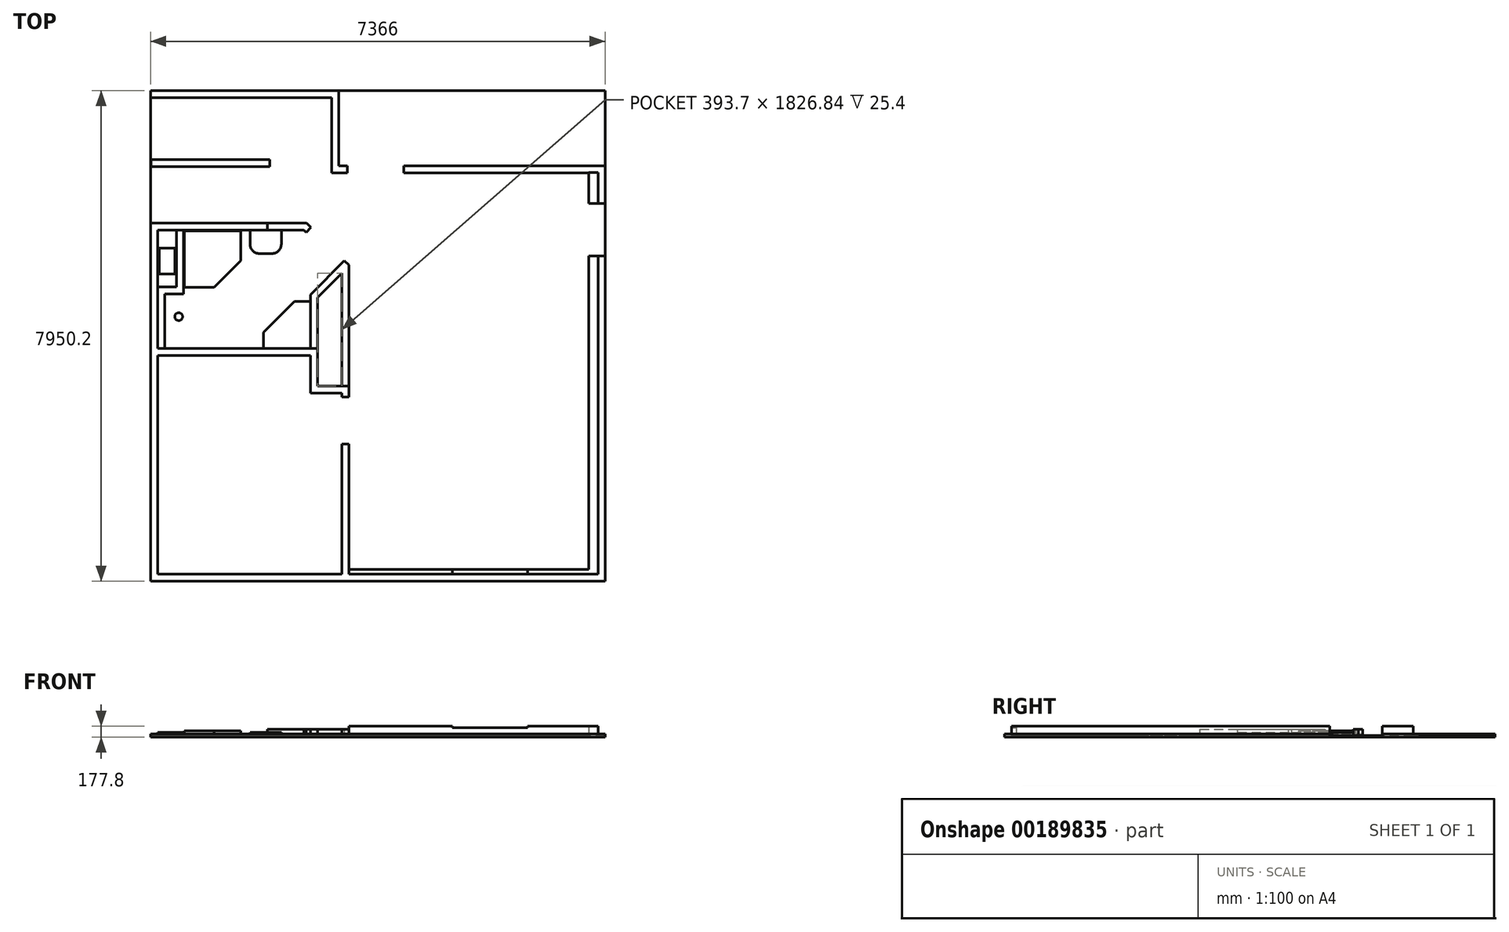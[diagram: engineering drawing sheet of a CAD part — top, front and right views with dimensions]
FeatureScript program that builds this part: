
annotation { "Feature Type Name" : "Feature", "Feature Type Description" : "" }
export const myFeature = defineFeature(function(context is Context, id is Id, definition is map)
    precondition{}
    {
        {
            var Q0;
            Q0=qCreatedBy(makeId("Top.planeOp"),FACE);
            var sketch = newSketch(context, id + "F0", { "sketchPlane" : qUnion([Q0])});
            skLineSegment(sketch, "E0.bottom", {"start": v(0, 0) * mm, "end": v(-7366, 0) * mm});
            skLineSegment(sketch, "E0.top", {"start": v(0, 7950.2) * mm, "end": v(-7366, 7950.2) * mm});
            skLineSegment(sketch, "E0.left", {"start": v(0, 0) * mm, "end": v(0, 7950.2) * mm});
            skLineSegment(sketch, "E0.right", {"start": v(-7366, 0) * mm, "end": v(-7366, 7950.2) * mm});
            skSolve(sketch);
        }
        {
            var Q0;
            Q0=qSketchRegion(id+"F0",true);
            extrude(context, id + "F1", {"entities" : qUnion([Q0]), "depth" : 25.4 * mm});
        }
        {
            var Q0;
            Q0=makeQuery(id+"F1.opExtrude","CAP_FACE",FACE,{"disambiguationData":[OSD([sQuery(id+"F0.wireOp",EDGE,"E0.bottom"),sQuery(id+"F0.wireOp",EDGE,"E0.top"),sQuery(id+"F0.wireOp",EDGE,"E0.left"),sQuery(id+"F0.wireOp",EDGE,"E0.right")])],"isStart":false});
            var sketch = newSketch(context, id + "F2", { "sketchPlane" : qUnion([Q0])});
            skLineSegment(sketch, "E1", {"start": v(0, 0) * mm, "end": v(0, 5270.5) * mm});
            skLineSegment(sketch, "E2", {"start": v(0, 5270.5) * mm, "end": v(-114.3, 5270.5) * mm});
            skLineSegment(sketch, "E3", {"start": v(-114.3, 5270.5) * mm, "end": v(-114.3, 114.3) * mm});
            skLineSegment(sketch, "E4", {"start": v(-114.3, 114.3) * mm, "end": v(-4152.9, 114.3) * mm});
            skLineSegment(sketch, "E5", {"start": v(-4152.9, 114.3) * mm, "end": v(-4152.9, 2222.5) * mm});
            skLineSegment(sketch, "E6", {"start": v(-4152.9, 2222.5) * mm, "end": v(-4267.2, 2222.5) * mm});
            skLineSegment(sketch, "E7", {"start": v(-4267.2, 2222.5) * mm, "end": v(-4267.2, 114.3) * mm});
            skLineSegment(sketch, "E8", {"start": v(-4267.2, 114.3) * mm, "end": v(-7251.7, 114.3) * mm});
            skLineSegment(sketch, "E9", {"start": v(0, 6121.4) * mm, "end": v(0, 6731) * mm});
            skLineSegment(sketch, "E10", {"start": v(0, 6731) * mm, "end": v(-3263.9, 6731) * mm});
            skLineSegment(sketch, "E11", {"start": v(0, 6121.4) * mm, "end": v(-114.3, 6121.4) * mm});
            skLineSegment(sketch, "E12", {"start": v(-114.3, 6121.4) * mm, "end": v(-114.3, 6616.7) * mm});
            skLineSegment(sketch, "E13", {"start": v(-114.3, 6616.7) * mm, "end": v(-3263.9, 6616.7) * mm});
            skLineSegment(sketch, "E14", {"start": v(-3263.9, 6731) * mm, "end": v(-3263.9, 6616.7) * mm});
            skLineSegment(sketch, "E15", {"start": v(-4152.9, 2984.5) * mm, "end": v(-4152.9, 3162.3) * mm});
            skLineSegment(sketch, "E16", {"start": v(-4152.9, 3162.3) * mm, "end": v(-4660.9, 3162.3) * mm});
            skLineSegment(sketch, "E17", {"start": v(-4660.9, 3162.3) * mm, "end": v(-4660.9, 3771.9) * mm});
            skLineSegment(sketch, "E18", {"start": v(-4660.9, 3771.9) * mm, "end": v(-7251.7, 3771.9) * mm});
            skLineSegment(sketch, "E19", {"start": v(-4152.9, 2984.5) * mm, "end": v(-4267.2, 2984.5) * mm});
            skLineSegment(sketch, "E20", {"start": v(-4267.2, 2984.5) * mm, "end": v(-4267.2, 3048) * mm});
            skLineSegment(sketch, "E21", {"start": v(-4267.2, 3048) * mm, "end": v(-4775.2, 3048) * mm});
            skLineSegment(sketch, "E22", {"start": v(-4775.2, 3048) * mm, "end": v(-4775.2, 3657.6) * mm});
            skLineSegment(sketch, "E23", {"start": v(-4775.2, 3657.6) * mm, "end": v(-7251.7, 3657.6) * mm});
            skLineSegment(sketch, "E24", {"start": v(-7251.7, 3771.9) * mm, "end": v(-7251.7, 5689.6) * mm});
            skLineSegment(sketch, "E25", {"start": v(-7251.7, 5689.6) * mm, "end": v(-5473.7, 5689.6) * mm});
            skLineSegment(sketch, "E26", {"start": v(-7366, 3657.6) * mm, "end": v(-7366, 5803.9) * mm});
            skLineSegment(sketch, "E27", {"start": v(-7366, 5803.9) * mm, "end": v(-5473.7, 5803.9) * mm});
            skLineSegment(sketch, "E28", {"start": v(-5473.7, 5689.6) * mm, "end": v(-5473.7, 5803.9) * mm});
            skLineSegment(sketch, "E29", {"start": v(-4178.3, 6616.7) * mm, "end": v(-4432.3, 6616.7) * mm});
            skLineSegment(sketch, "E30", {"start": v(-4432.3, 6616.7) * mm, "end": v(-4432.3, 7835.9) * mm});
            skLineSegment(sketch, "E31", {"start": v(-4432.3, 7835.9) * mm, "end": v(-7362.92, 7835.9) * mm});
            skLineSegment(sketch, "E32", {"start": v(-4178.3, 6616.7) * mm, "end": v(-4178.3, 6731) * mm});
            skLineSegment(sketch, "E33", {"start": v(-4178.3, 6731) * mm, "end": v(-4318, 6731) * mm});
            skLineSegment(sketch, "E34", {"start": v(-4318, 6731) * mm, "end": v(-4318, 7950.2) * mm});
            skLineSegment(sketch, "E35", {"start": v(-4318, 7950.2) * mm, "end": v(-7362.92, 7950.2) * mm});
            skLineSegment(sketch, "E36.bottom", {"start": v(-7359.96, 6832.6) * mm, "end": v(-5435.6, 6832.6) * mm});
            skLineSegment(sketch, "E36.top", {"start": v(-7359.96, 6718.3) * mm, "end": v(-5435.6, 6718.3) * mm});
            skLineSegment(sketch, "E36.left", {"start": v(-7359.96, 6832.6) * mm, "end": v(-7359.96, 6718.3) * mm});
            skLineSegment(sketch, "E36.right", {"start": v(-5435.6, 6832.6) * mm, "end": v(-5435.6, 6718.3) * mm});
            skLineSegment(sketch, "E37", {"start": v(-7362.92, 7835.9) * mm, "end": v(-7362.92, 7950.2) * mm});
            skPoint(sketch, "E38.orphan", {"position": v(-6077.52, 7950.2) * mm});
            skLineSegment(sketch, "E39", {"start": v(0, 0) * mm, "end": v(-7366, 0) * mm});
            skLineSegment(sketch, "E40", {"start": v(-7366, 0) * mm, "end": v(-7366, 3657.6) * mm});
            skLineSegment(sketch, "E41", {"start": v(-7251.7, 114.3) * mm, "end": v(-7251.7, 3657.6) * mm});
            skSolve(sketch);
        }
        {
            var Q0;
            Q0=qSketchRegion(id+"F2",true);
            extrude(context, id + "F3", {"entities" : qUnion([Q0]), "operationType" : NewBodyOperationType.ADD, "depth" : 25.4 * mm});
        }
        {
            var Q0;
            Q0=makeQuery(id+"F1.opExtrude","CAP_FACE",FACE,{"disambiguationData":[OSD([sQuery(id+"F0.wireOp",EDGE,"E0.bottom"),sQuery(id+"F0.wireOp",EDGE,"E0.top"),sQuery(id+"F0.wireOp",EDGE,"E0.left"),sQuery(id+"F0.wireOp",EDGE,"E0.right")])],"isStart":false});
            var sketch = newSketch(context, id + "F4", { "sketchPlane" : qUnion([Q0])});
            skCircle(sketch, "E42", {"center": v(-6908.8, 4286.25) * mm, "radius": 63.5 * mm});
            skLineSegment(sketch, "E43.bottom", {"start": v(-7226.3, 5397.5) * mm, "end": v(-6972.3, 5397.5) * mm});
            skLineSegment(sketch, "E43.top", {"start": v(-7226.3, 4978.4) * mm, "end": v(-6972.3, 4978.4) * mm});
            skLineSegment(sketch, "E43.left", {"start": v(-7226.3, 5397.5) * mm, "end": v(-7226.3, 4978.4) * mm});
            skLineSegment(sketch, "E43.right", {"start": v(-6972.3, 5397.5) * mm, "end": v(-6972.3, 4978.4) * mm});
            skCircle(sketch, "E44", {"center": v(-7200.9, 4692.65) * mm, "radius": 44.45 * mm});
            skSolve(sketch);
        }
        {
            var Q0;
            Q0=qSketchRegion(id+"F4",true);
            extrude(context, id + "F5", {"entities" : qUnion([Q0]), "operationType" : NewBodyOperationType.ADD, "depth" : 25.4 * mm});
        }
        {
            var Q0;
            Q0=makeQuery(id+"F1.opExtrude","CAP_FACE",FACE,{"disambiguationData":[OSD([sQuery(id+"F0.wireOp",EDGE,"E0.bottom"),sQuery(id+"F0.wireOp",EDGE,"E0.top"),sQuery(id+"F0.wireOp",EDGE,"E0.left"),sQuery(id+"F0.wireOp",EDGE,"E0.right")])],"isStart":false});
            var sketch = newSketch(context, id + "F6", { "sketchPlane" : qUnion([Q0])});
            skLineSegment(sketch, "E45", {"start": v(-6946.9, 5689.6) * mm, "end": v(-6946.9, 4768.85) * mm});
            skLineSegment(sketch, "E46", {"start": v(-6946.9, 4768.85) * mm, "end": v(-7251.7, 4768.85) * mm});
            skLineSegment(sketch, "E47", {"start": v(-7251.7, 4768.85) * mm, "end": v(-7251.7, 3771.9) * mm});
            skLineSegment(sketch, "E48", {"start": v(-7251.7, 3771.9) * mm, "end": v(-7137.4, 3771.9) * mm});
            skLineSegment(sketch, "E49", {"start": v(-7137.4, 3771.9) * mm, "end": v(-7137.4, 4654.55) * mm});
            skLineSegment(sketch, "E50", {"start": v(-7137.4, 4654.55) * mm, "end": v(-6832.6, 4654.55) * mm});
            skLineSegment(sketch, "E51", {"start": v(-6832.6, 4654.55) * mm, "end": v(-6832.6, 5689.6) * mm});
            skLineSegment(sketch, "E52", {"start": v(-6832.6, 5689.6) * mm, "end": v(-6946.9, 5689.6) * mm});
            skSolve(sketch);
        }
        {
            var Q0;
            Q0=qSketchRegion(id+"F6",true);
            extrude(context, id + "F7", {"entities" : qUnion([Q0]), "operationType" : NewBodyOperationType.ADD, "depth" : 50.8 * mm});
        }
        {
            var Q0;
            {var subQ0=sQuery(id+"F0.wireOp",EDGE,"E0.left");var subQ1=sQuery(id+"F0.wireOp",EDGE,"E0.top");var subQ2=sQuery(id+"F0.wireOp",EDGE,"E0.right");Q0=makeQuery(id+"F7.boolean.opBoolean","SPLIT",FACE,{"disambiguationData":[TD([makeQuery(id+"F1.opExtrude","SWEPT_FACE",FACE,{"disambiguationData":[OSD([subQ1])]})])],"derivedFrom":makeQuery(id+"F1.opExtrude","CAP_FACE",FACE,{"disambiguationData":[OSD([sQuery(id+"F0.wireOp",EDGE,"E0.bottom"),subQ1,subQ0,subQ2])],"isStart":false})});}
            var sketch = newSketch(context, id + "F8", { "sketchPlane" : qUnion([Q0])});
            skLineSegment(sketch, "E53", {"start": v(-6819.9, 5676.9) * mm, "end": v(-5905.5, 5676.9) * mm});
            skLineSegment(sketch, "E54", {"start": v(-5905.5, 5676.9) * mm, "end": v(-5905.5, 5194.3) * mm});
            skLineSegment(sketch, "E55", {"start": v(-5905.5, 5194.3) * mm, "end": v(-6337.3, 4762.5) * mm});
            skLineSegment(sketch, "E56", {"start": v(-6337.3, 4762.5) * mm, "end": v(-6819.9, 4762.5) * mm});
            skLineSegment(sketch, "E57", {"start": v(-6819.9, 4762.5) * mm, "end": v(-6819.9, 5676.9) * mm});
            skSolve(sketch);
        }
        {
            var Q0;
            Q0=qSketchRegion(id+"F8",true);
            extrude(context, id + "F9", {"entities" : qUnion([Q0]), "operationType" : NewBodyOperationType.ADD, "depth" : 76.2 * mm});
        }
        {
            var Q0;
            {var subQ0=sQuery(id+"F0.wireOp",EDGE,"E0.left");var subQ1=sQuery(id+"F0.wireOp",EDGE,"E0.top");var subQ2=sQuery(id+"F0.wireOp",EDGE,"E0.right");Q0=makeQuery(id+"F7.boolean.opBoolean","SPLIT",FACE,{"disambiguationData":[TD([makeQuery(id+"F1.opExtrude","SWEPT_FACE",FACE,{"disambiguationData":[OSD([subQ1])]})])],"derivedFrom":makeQuery(id+"F1.opExtrude","CAP_FACE",FACE,{"disambiguationData":[OSD([sQuery(id+"F0.wireOp",EDGE,"E0.bottom"),subQ1,subQ0,subQ2])],"isStart":false})});}
            var sketch = newSketch(context, id + "F10", { "sketchPlane" : qUnion([Q0])});
            skLineSegment(sketch, "E58", {"start": v(-5473.7, 5689.6) * mm, "end": v(-4882.74, 5689.6) * mm});
            skLineSegment(sketch, "E59", {"start": v(-4775.2, 3771.9) * mm, "end": v(-4775.2, 4597.4) * mm});
            skLineSegment(sketch, "E60", {"start": v(-5473.7, 5689.6) * mm, "end": v(-5473.7, 5803.9) * mm});
            skLineSegment(sketch, "E61", {"start": v(-5473.7, 5803.9) * mm, "end": v(-4835.4, 5803.9) * mm});
            skLineSegment(sketch, "E62", {"start": v(-4775.2, 3771.9) * mm, "end": v(-4660.9, 3771.9) * mm});
            skLineSegment(sketch, "E63", {"start": v(-4660.9, 3771.9) * mm, "end": v(-4660.9, 4595.44) * mm});
            skLineSegment(sketch, "E64", {"start": v(-4152.9, 3162.3) * mm, "end": v(-4152.9, 5105.4) * mm});
            skLineSegment(sketch, "E65", {"start": v(-4152.9, 3162.3) * mm, "end": v(-4267.2, 3162.3) * mm});
            skLineSegment(sketch, "E66", {"start": v(-4267.2, 3162.3) * mm, "end": v(-4267.2, 4991.1) * mm});
            skLineSegment(sketch, "E67", {"start": v(-4152.9, 5105.4) * mm, "end": v(-4152.9, 5121.4) * mm});
            skLineSegment(sketch, "E68", {"start": v(-4152.9, 5121.4) * mm, "end": v(-4224.74, 5193.24) * mm});
            skLineSegment(sketch, "E69", {"start": v(-4882.74, 5689.6) * mm, "end": v(-4844.38, 5651.24) * mm});
            skLineSegment(sketch, "E70", {"start": v(-4844.38, 5651.24) * mm, "end": v(-4763.56, 5732.06) * mm});
            skLineSegment(sketch, "E71", {"start": v(-4305.56, 5112.42) * mm, "end": v(-4224.74, 5193.24) * mm});
            skLineSegment(sketch, "E72.trimOffspring", {"start": v(-4763.56, 5732.06) * mm, "end": v(-4835.4, 5803.9) * mm});
            skLineSegment(sketch, "E73", {"start": v(-4775.2, 4597.4) * mm, "end": v(-4775.2, 4642.78) * mm});
            skLineSegment(sketch, "E74", {"start": v(-4265.24, 4991.1) * mm, "end": v(-4267.2, 4991.1) * mm});
            skLineSegment(sketch, "E75", {"start": v(-4305.56, 5112.42) * mm, "end": v(-4775.2, 4642.78) * mm});
            skLineSegment(sketch, "E76", {"start": v(-4660.9, 4595.44) * mm, "end": v(-4152.9, 5103.44) * mm});
            skSolve(sketch);
        }
        {
            var Q0;
            Q0=qSketchRegion(id+"F10",true);
            extrude(context, id + "F11", {"entities" : qUnion([Q0]), "operationType" : NewBodyOperationType.ADD, "depth" : 101.6 * mm});
        }
        {
            var Q0;
            {var subQ29=sQuery(id+"F0.wireOp",EDGE,"E0.left");var subQ32=sQuery(id+"F0.wireOp",EDGE,"E0.top");var subQ33=makeQuery(id+"F1.opExtrude","SWEPT_FACE",FACE,{"disambiguationData":[OSD([subQ32])]});var subQ34=sQuery(id+"F0.wireOp",EDGE,"E0.right");Q0=makeQuery(id+"F11.boolean.opBoolean","SPLIT",FACE,{"disambiguationData":[TD([subQ33])],"derivedFrom":makeQuery(id+"F7.boolean.opBoolean","SPLIT",FACE,{"disambiguationData":[TD([subQ33])],"derivedFrom":makeQuery(id+"F1.opExtrude","CAP_FACE",FACE,{"disambiguationData":[OSD([sQuery(id+"F0.wireOp",EDGE,"E0.bottom"),subQ32,subQ29,subQ34])],"isStart":false})})});}
            var sketch = newSketch(context, id + "F12", { "sketchPlane" : qUnion([Q0])});
            skLineSegment(sketch, "E77.bottom", {"start": v(-4775.2, 3771.9) * mm, "end": v(-5537.2, 3771.9) * mm});
            skLineSegment(sketch, "E77.top", {"start": v(-4775.2, 4533.9) * mm, "end": v(-5034.3, 4533.9) * mm});
            skLineSegment(sketch, "E77.left", {"start": v(-4775.2, 3771.9) * mm, "end": v(-4775.2, 4533.9) * mm});
            skLineSegment(sketch, "E77.right", {"start": v(-5537.2, 3771.9) * mm, "end": v(-5537.2, 4031) * mm});
            skLineSegment(sketch, "E78", {"start": v(-5537.2, 4031) * mm, "end": v(-5034.3, 4533.9) * mm});
            skSolve(sketch);
        }
        {
            var Q0;
            Q0=qSketchRegion(id+"F12",true);
            extrude(context, id + "F13", {"entities" : qUnion([Q0]), "operationType" : NewBodyOperationType.ADD, "depth" : 12.7 * mm});
        }
        {
            var Q0;
            {var subQ29=sQuery(id+"F0.wireOp",EDGE,"E0.left");var subQ32=sQuery(id+"F0.wireOp",EDGE,"E0.top");var subQ33=makeQuery(id+"F1.opExtrude","SWEPT_FACE",FACE,{"disambiguationData":[OSD([subQ32])]});var subQ34=sQuery(id+"F0.wireOp",EDGE,"E0.right");Q0=makeQuery(id+"F11.boolean.opBoolean","SPLIT",FACE,{"disambiguationData":[TD([subQ33])],"derivedFrom":makeQuery(id+"F7.boolean.opBoolean","SPLIT",FACE,{"disambiguationData":[TD([subQ33])],"derivedFrom":makeQuery(id+"F1.opExtrude","CAP_FACE",FACE,{"disambiguationData":[OSD([sQuery(id+"F0.wireOp",EDGE,"E0.bottom"),subQ32,subQ29,subQ34])],"isStart":false})})});}
            var sketch = newSketch(context, id + "F14", { "sketchPlane" : qUnion([Q0])});
            skLineSegment(sketch, "E79", {"start": v(-6426.2, 4354.08) * mm, "end": v(-6426.2, 4192.23) * mm, "construction": true});
            skSolve(sketch);
        }
        {
            var Q0;
            {var subQ2=sQuery(id+"F0.wireOp",EDGE,"E0.right");Q0=makeQuery(id+"F14.imprint","IMPRINT",FACE,{"disambiguationData":[TD([[makeQuery(id+"F14.imprint","IMPRINT",EDGE,{"derivedFrom":makeQuery(id+"F1.opExtrude","CAP_EDGE",EDGE,{"disambiguationData":[OSD([subQ2])],"isStart":false})}),-1.0]])]});}
            var sketch = newSketch(context, id + "F15", { "sketchPlane" : qUnion([Q0])});
            skLineSegment(sketch, "E80.bottom", {"start": v(-5753.1, 5689.6) * mm, "end": v(-5245.1, 5689.6) * mm});
            skLineSegment(sketch, "E80.top", {"start": v(-5600.7, 5308.6) * mm, "end": v(-5397.5, 5308.6) * mm});
            skLineSegment(sketch, "E80.left", {"start": v(-5753.1, 5689.6) * mm, "end": v(-5753.1, 5461) * mm});
            skLineSegment(sketch, "E80.right", {"start": v(-5245.1, 5689.6) * mm, "end": v(-5245.1, 5461) * mm});
            skPoint(sketch, "E81.visualSharp", {"position": v(-5245.1, 5308.6) * mm});
            skArc(sketch, "E81.filletArc", {"start": v(-5397.5, 5308.6) * mm, "mid": v(-5289.74, 5353.24) * mm, "end": v(-5245.1, 5461) * mm});
            skPoint(sketch, "E82.visualSharp", {"position": v(-5753.1, 5308.6) * mm});
            skArc(sketch, "E82.filletArc", {"start": v(-5753.1, 5461) * mm, "mid": v(-5708.46, 5353.24) * mm, "end": v(-5600.7, 5308.6) * mm});
            skSolve(sketch);
        }
        {
            var Q0;
            Q0=qSketchRegion(id+"F15",true);
            extrude(context, id + "F16", {"entities" : qUnion([Q0]), "operationType" : NewBodyOperationType.ADD, "depth" : 50.8 * mm});
        }
        {
            var Q0;
            {var subQ2=sQuery(id+"F0.wireOp",EDGE,"E0.right");Q0=makeQuery(id+"F14.imprint","IMPRINT",FACE,{"disambiguationData":[TD([[makeQuery(id+"F14.imprint","IMPRINT",EDGE,{"derivedFrom":makeQuery(id+"F1.opExtrude","CAP_EDGE",EDGE,{"disambiguationData":[OSD([subQ2])],"isStart":false})}),-1.0]])]});}
            var sketch = newSketch(context, id + "F17", { "sketchPlane" : qUnion([Q0])});
            skLineSegment(sketch, "E83.bottom", {"start": v(-4152.9, 190.5) * mm, "end": v(-266.7, 190.5) * mm});
            skLineSegment(sketch, "E83.top", {"start": v(-4152.9, 114.3) * mm, "end": v(-114.3, 114.3) * mm});
            skLineSegment(sketch, "E83.left", {"start": v(-4152.9, 190.5) * mm, "end": v(-4152.9, 114.3) * mm});
            skLineSegment(sketch, "E83.right", {"start": v(-114.3, 190.5) * mm, "end": v(-114.3, 114.3) * mm});
            skLineSegment(sketch, "E84.bottom", {"start": v(-266.7, 6621.26) * mm, "end": v(-114.3, 6621.26) * mm});
            skLineSegment(sketch, "E84.left", {"start": v(-266.7, 6621.26) * mm, "end": v(-266.7, 6121.4) * mm});
            skLineSegment(sketch, "E84.right", {"start": v(-114.3, 6621.26) * mm, "end": v(-114.3, 6121.4) * mm});
            skLineSegment(sketch, "E85", {"start": v(-114.3, 5270.5) * mm, "end": v(-266.7, 5270.5) * mm});
            skLineSegment(sketch, "E86", {"start": v(-114.3, 6121.4) * mm, "end": v(-266.7, 6121.4) * mm});
            skLineSegment(sketch, "E87.trimOffspring", {"start": v(-266.7, 5270.5) * mm, "end": v(-266.7, 190.5) * mm});
            skLineSegment(sketch, "E88.trimOffspring", {"start": v(-114.3, 5270.5) * mm, "end": v(-114.3, 190.5) * mm});
            skSolve(sketch);
        }
        {
            var Q0;
            Q0 = qSketchRegion(id + "F17", true);
            extrude(context, id + "F18", {"entities" : qUnion([Q0]), "operationType" : NewBodyOperationType.ADD, "depth" : 152.4 * mm});
        }
        {
            var Q0;
            Q0=makeQuery(id+"F18.opExtrude","CAP_FACE",FACE,{"disambiguationData":[OSD([sQuery(id+"F17.wireOp",EDGE,"E83.bottom"),sQuery(id+"F17.wireOp",EDGE,"E83.top"),sQuery(id+"F17.wireOp",EDGE,"E83.left"),sQuery(id+"F17.wireOp",EDGE,"E83.right"),sQuery(id+"F17.wireOp",EDGE,"E85"),sQuery(id+"F17.wireOp",EDGE,"E87.trimOffspring"),sQuery(id+"F17.wireOp",EDGE,"E88.trimOffspring")])],"isStart":false});
            var sketch = newSketch(context, id + "F19", { "sketchPlane" : qUnion([Q0])});
            skLineSegment(sketch, "E89.bottom", {"start": v(-1257.3, 114.3) * mm, "end": v(-2476.5, 114.3) * mm});
            skLineSegment(sketch, "E89.top", {"start": v(-1257.3, 190.5) * mm, "end": v(-2476.5, 190.5) * mm});
            skLineSegment(sketch, "E89.left", {"start": v(-1257.3, 114.3) * mm, "end": v(-1257.3, 190.5) * mm});
            skLineSegment(sketch, "E89.right", {"start": v(-2476.5, 114.3) * mm, "end": v(-2476.5, 190.5) * mm});
            skSolve(sketch);
        }
        {
            var Q0;
            Q0 = qSketchRegion(id + "F19", true);
            extrude(context, id + "F20", {"entities" : qUnion([Q0]), "operationType" : NewBodyOperationType.REMOVE, "oppositeDirection" : true, "depth" : 25.4 * mm});
        }
    });
